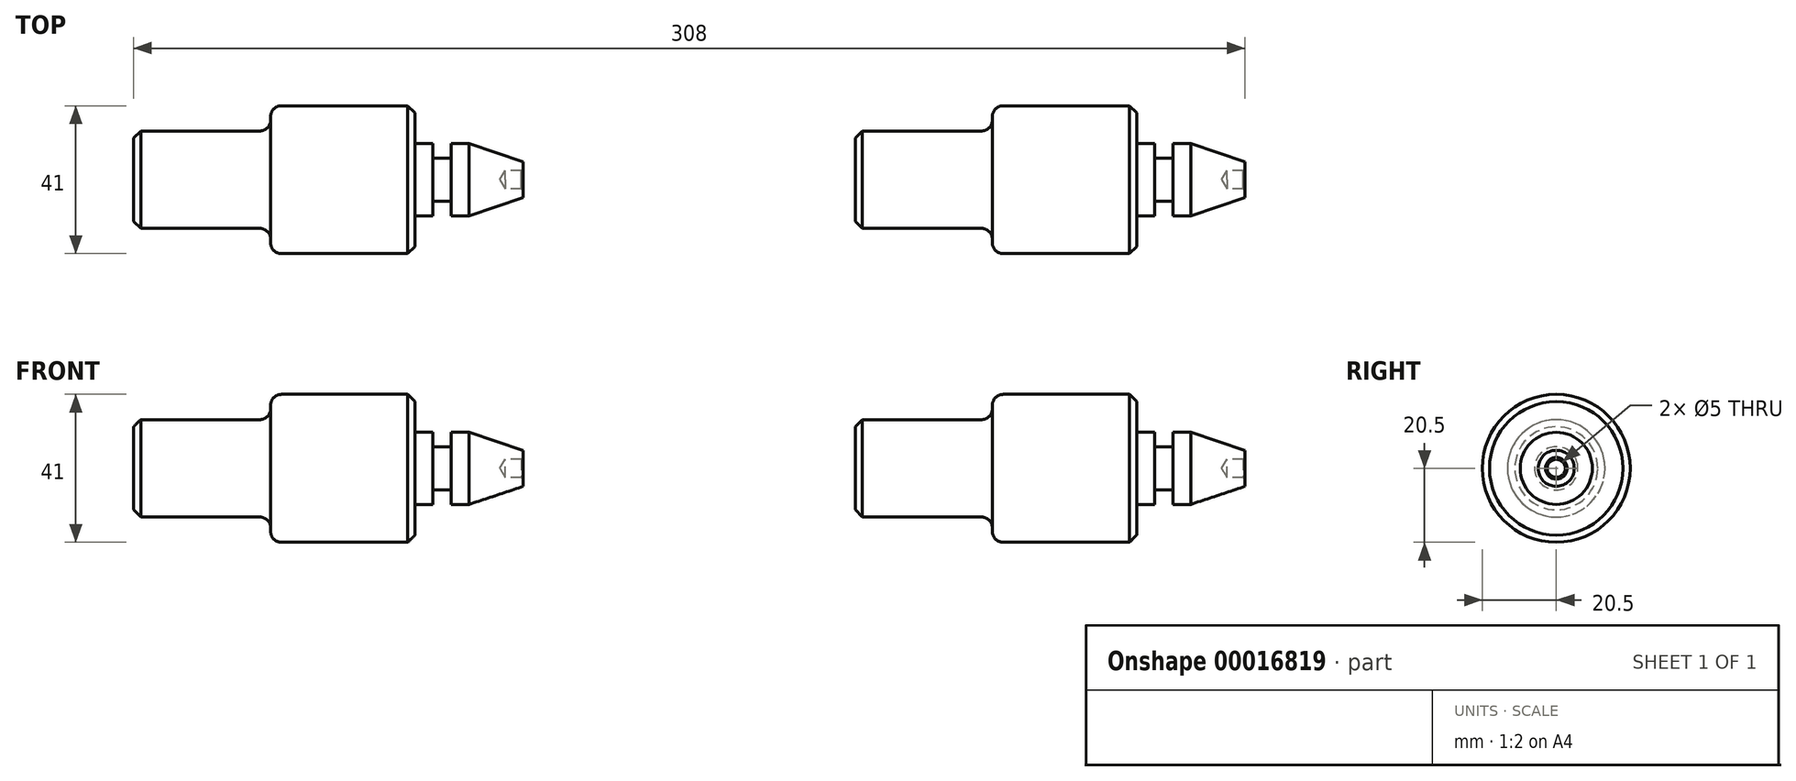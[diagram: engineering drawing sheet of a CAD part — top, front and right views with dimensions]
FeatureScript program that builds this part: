
annotation { "Feature Type Name" : "Feature", "Feature Type Description" : "" }
export const myFeature = defineFeature(function(context is Context, id is Id, definition is map)
    precondition{}
    {
        {
            var Q0;
            Q0=qCreatedBy(makeId("Top.planeOp"),FACE);
            var sketch = newSketch(context, id + "F0", { "sketchPlane" : qUnion([Q0])});
            skLineSegment(sketch, "E0", {"start": v(0, 0) * mm, "end": v(0, 5) * mm});
            skLineSegment(sketch, "E1", {"start": v(-73, 13.5) * mm, "end": v(-108, 13.5) * mm});
            skLineSegment(sketch, "E2", {"start": v(-108, 13.5) * mm, "end": v(-108, 0) * mm});
            skLineSegment(sketch, "E3", {"start": v(0, 0) * mm, "end": v(-108, 0) * mm});
            skLineSegment(sketch, "E4", {"start": v(0, 5) * mm, "end": v(-15, 10) * mm});
            skLineSegment(sketch, "E5", {"start": v(-15, 10) * mm, "end": v(-20, 10) * mm});
            skLineSegment(sketch, "E6", {"start": v(-20, 10) * mm, "end": v(-20, 6) * mm});
            skLineSegment(sketch, "E7", {"start": v(-20, 6) * mm, "end": v(-25, 6) * mm});
            skLineSegment(sketch, "E8", {"start": v(-25, 6) * mm, "end": v(-25, 10) * mm});
            skLineSegment(sketch, "E9", {"start": v(-25, 10) * mm, "end": v(-30, 10) * mm});
            skLineSegment(sketch, "E10", {"start": v(-30, 10) * mm, "end": v(-30, 20.5) * mm});
            skLineSegment(sketch, "E11", {"start": v(-30, 20.5) * mm, "end": v(-67, 20.5) * mm});
            skLineSegment(sketch, "E12", {"start": v(-70, 17.5) * mm, "end": v(-70, 16.5) * mm});
            skPoint(sketch, "E13.visualSharp", {"position": v(-70, 20.5) * mm});
            skArc(sketch, "E13.filletArc", {"start": v(-67, 20.5) * mm, "mid": v(-69.12, 19.62) * mm, "end": v(-70, 17.5) * mm});
            skPoint(sketch, "E14.visualSharp", {"position": v(-70, 13.5) * mm});
            skArc(sketch, "E14.filletArc", {"start": v(-73, 13.5) * mm, "mid": v(-70.88, 14.38) * mm, "end": v(-70, 16.5) * mm});
            skSolve(sketch);
        }
        {
            var Q0;
            Q0=makeQuery(id+"F0.imprint","IMPRINT",FACE,{"disambiguationData":[TD([[makeQuery(id+"F0.imprint","IMPRINT",EDGE,{"derivedFrom":sQuery(id+"F0.wireOp",EDGE,"E0")}),1.0]])]});
            var Q1;
            Q1=sQuery(id+"F0.wireOp",EDGE,"E3");
            revolve(context, id + "F1", {"entities" : qUnion([Q0]), "axis" : qUnion([Q1]), "revolveType" : RevolveType.FULL});
        }
        {
            var Q0;
            Q0=makeQuery(id+"F1.opRevolve","SWEPT_FACE",FACE,{"disambiguationData":[OSD([sQuery(id+"F0.wireOp",EDGE,"E0")])]});
            var sketch = newSketch(context, id + "F2", { "sketchPlane" : qUnion([Q0])});
            skCircle(sketch, "E15", {"center": v(0, 0) * mm, "radius": 2.5 * mm});
            skSolve(sketch);
        }
        {
            var Q0;
            Q0=sQuery(id+"F2.wireOp",VERTEX,"E15.center");
            var Q1;
            Q1=makeQuery(id+"F1.opRevolve","SWEPT_BODY",BODY,{"disambiguationData":[OSD([sQuery(id+"F0.wireOp",EDGE,"E0"),sQuery(id+"F0.wireOp",EDGE,"E1"),sQuery(id+"F0.wireOp",EDGE,"E2"),sQuery(id+"F0.wireOp",EDGE,"E3"),sQuery(id+"F0.wireOp",EDGE,"E4"),sQuery(id+"F0.wireOp",EDGE,"E5"),sQuery(id+"F0.wireOp",EDGE,"E6"),sQuery(id+"F0.wireOp",EDGE,"E7"),sQuery(id+"F0.wireOp",EDGE,"E8"),sQuery(id+"F0.wireOp",EDGE,"E9"),sQuery(id+"F0.wireOp",EDGE,"E10"),sQuery(id+"F0.wireOp",EDGE,"E11"),sQuery(id+"F0.wireOp",EDGE,"E12")])]});
            hole(context, id + "F3", {"style" : HoleStyle.C_SINK, "holeDiameter" : 5 * mm, "cSinkDiameter" : 6 * mm, "endStyle" : HoleEndStyle.BLIND, "holeDepth" : 5 * mm, "locations" : qUnion([Q0]), "scope" : qUnion([Q1]), "cSinkAngle" : 90 * degree});
        }
        {
            var Q0;
            Q0=makeQuery(id+"F1.opRevolve","SWEPT_EDGE",EDGE,{"disambiguationData":[OSD([sQuery(id+"F0.wireOp",EDGE,"E1"),sQuery(id+"F0.wireOp",EDGE,"E2")])]});
            var Q1;
            Q1=makeQuery(id+"F1.opRevolve","SWEPT_EDGE",EDGE,{"disambiguationData":[OSD([sQuery(id+"F0.wireOp",EDGE,"E11"),sQuery(id+"F0.wireOp",EDGE,"E12")])]});
            var Q2;
            Q2=makeQuery(id+"F1.opRevolve","SWEPT_EDGE",EDGE,{"disambiguationData":[OSD([sQuery(id+"F0.wireOp",EDGE,"E10"),sQuery(id+"F0.wireOp",EDGE,"E11")])]});
            chamfer(context, id + "F4", {"entities" : qUnion([Q0, Q1, Q2]), "width" : 2 * mm, "tangentPropagation" : true});
        }
        {
            var Q0;
            Q0=makeQuery(id+"F1.opRevolve","SWEPT_BODY",BODY,{"disambiguationData":[OSD([sQuery(id+"F0.wireOp",EDGE,"E0"),sQuery(id+"F0.wireOp",EDGE,"E1"),sQuery(id+"F0.wireOp",EDGE,"E2"),sQuery(id+"F0.wireOp",EDGE,"E3"),sQuery(id+"F0.wireOp",EDGE,"E4"),sQuery(id+"F0.wireOp",EDGE,"E5"),sQuery(id+"F0.wireOp",EDGE,"E6"),sQuery(id+"F0.wireOp",EDGE,"E7"),sQuery(id+"F0.wireOp",EDGE,"E8"),sQuery(id+"F0.wireOp",EDGE,"E9"),sQuery(id+"F0.wireOp",EDGE,"E10"),sQuery(id+"F0.wireOp",EDGE,"E11"),sQuery(id+"F0.wireOp",EDGE,"E12"),sQuery(id+"F0.wireOp",EDGE,"E13.filletArc"),sQuery(id+"F0.wireOp",EDGE,"E14.filletArc")])]});
            transform(context, id + "F5", {"entities" : qUnion([Q0]), "transformType" : TransformType.TRANSLATION_3D, "dx" : 200 * mm, "dy" : 0 * mm, "dz" : 0 * mm, "makeCopy" : true});
        }
    });
